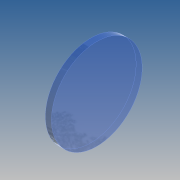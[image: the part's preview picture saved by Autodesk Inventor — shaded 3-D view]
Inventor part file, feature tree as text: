
AUTODESK INVENTOR PART (.ipt)
format: ipt  version: 2019 (Build 230136000, 136)  size: 200,704 bytes
history: native  units: mm
features: revolve x1, sketch x1
ambient origin geometry x8: Origin, YZ Plane, XZ Plane, XY Plane, X Axis, Y Axis, Z Axis, Center Point
bodies: Solid1 (feature_tree)
feature tree (2):
  revolve  "Revolution1"  [1 undecoded]
  sketch  "Sketch1"  dims[d0=30.0mm d1=2.0mm d2=4.5mm d3=90.0deg]
note: 1 required parameter value undecoded (feature->parameter linkage not recoverable at this tier; creation-order binding heuristic only, values carry confidence <= 0.55)
